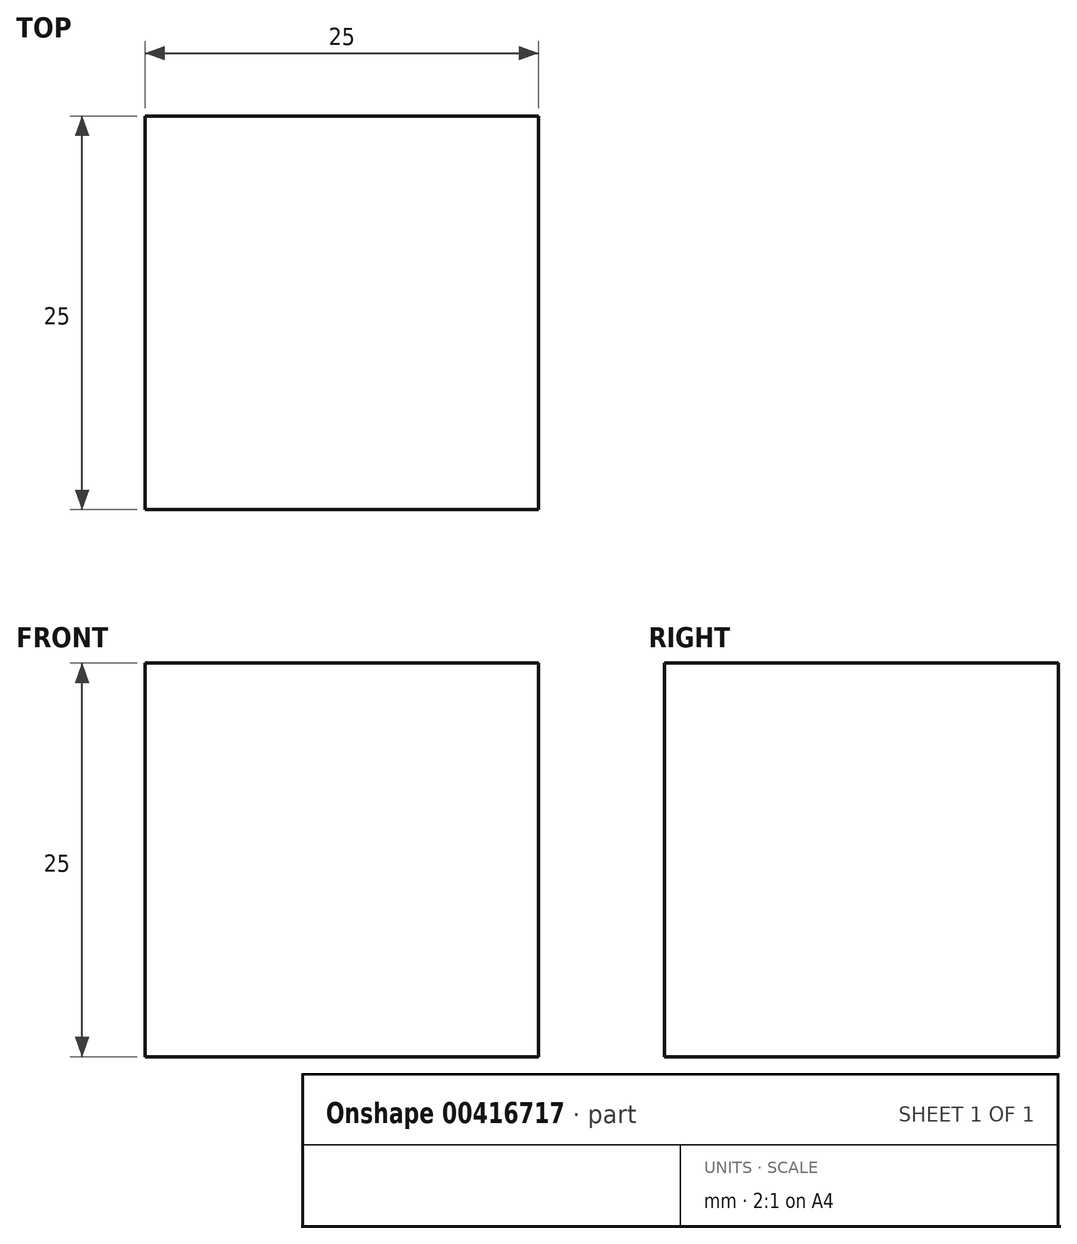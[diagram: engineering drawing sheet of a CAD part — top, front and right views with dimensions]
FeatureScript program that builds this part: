
annotation { "Feature Type Name" : "Feature", "Feature Type Description" : "" }
export const myFeature = defineFeature(function(context is Context, id is Id, definition is map)
    precondition{}
    {
        {
            var Q0;
            Q0=qCreatedBy(makeId("Top.planeOp"),FACE);
            var sketch = newSketch(context, id + "F0", { "sketchPlane" : qUnion([Q0])});
            skLineSegment(sketch, "E0.bottom", {"start": v(0, 0) * mm, "end": v(-25, 0) * mm});
            skLineSegment(sketch, "E0.top", {"start": v(0, 25) * mm, "end": v(-25, 25) * mm});
            skLineSegment(sketch, "E0.left", {"start": v(0, 0) * mm, "end": v(0, 25) * mm});
            skLineSegment(sketch, "E0.right", {"start": v(-25, 0) * mm, "end": v(-25, 25) * mm});
            skSolve(sketch);
        }
        {
            var Q0;
            Q0=makeQuery(id+"F0.imprint","IMPRINT",FACE,{"disambiguationData":[TD([[makeQuery(id+"F0.imprint","IMPRINT",EDGE,{"derivedFrom":sQuery(id+"F0.wireOp",EDGE,"E0.bottom")}),-1.0]])]});
            extrude(context, id + "F1", {"entities" : qUnion([Q0]), "depth" : 25 * mm});
        }
    });
